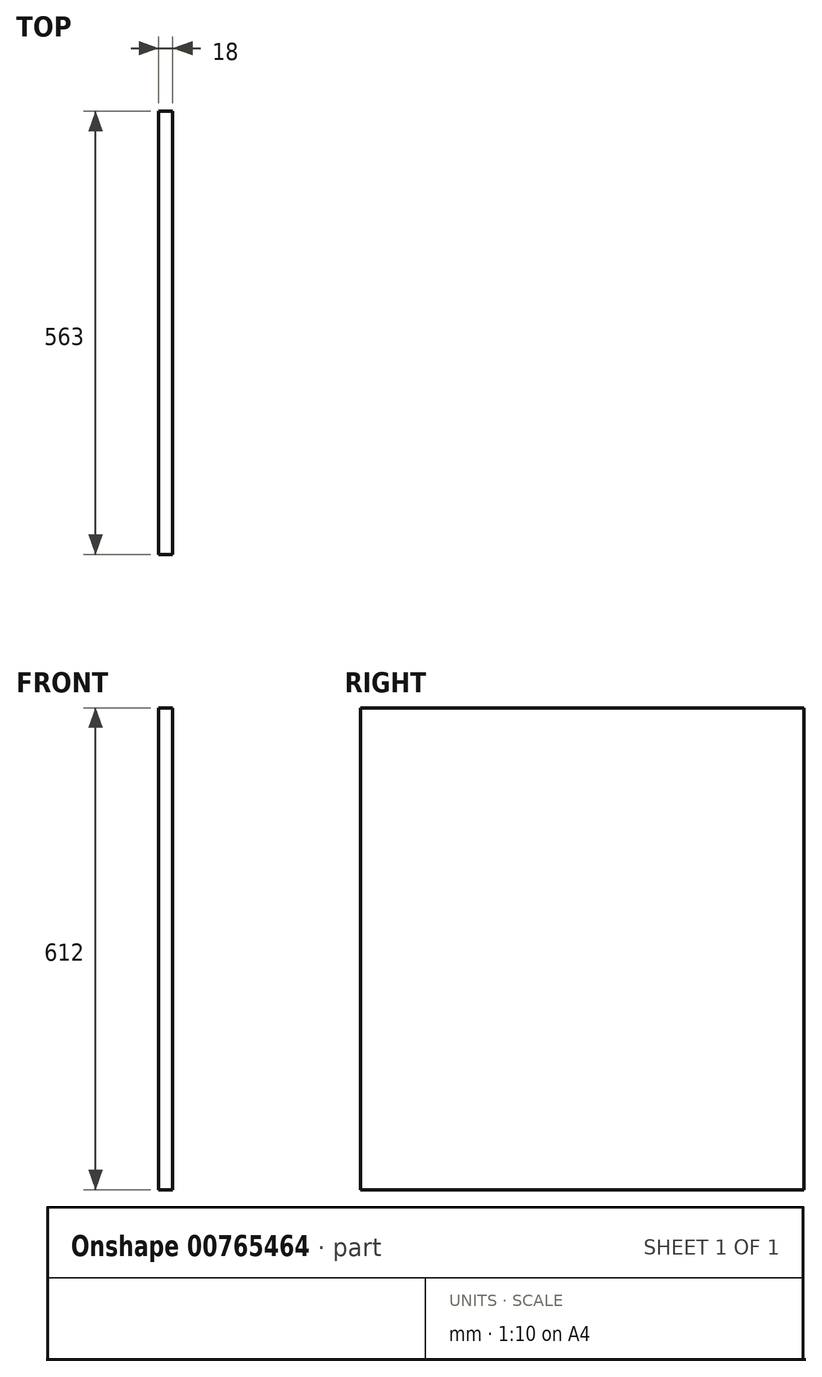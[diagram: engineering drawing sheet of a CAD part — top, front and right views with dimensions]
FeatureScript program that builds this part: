
annotation { "Feature Type Name" : "Feature", "Feature Type Description" : "" }
export const myFeature = defineFeature(function(context is Context, id is Id, definition is map)
    precondition{}
    {
        {
            var Q0;
            Q0=qCreatedBy(makeId("Right.planeOp"),FACE);
            var sketch = newSketch(context, id + "F0", { "sketchPlane" : qUnion([Q0])});
            skLineSegment(sketch, "E0.bottom", {"start": v(-281.5, 306) * mm, "end": v(281.5, 306) * mm});
            skLineSegment(sketch, "E0.top", {"start": v(-281.5, -306) * mm, "end": v(281.5, -306) * mm});
            skLineSegment(sketch, "E0.left", {"start": v(-281.5, 306) * mm, "end": v(-281.5, -306) * mm});
            skLineSegment(sketch, "E0.right", {"start": v(281.5, 306) * mm, "end": v(281.5, -306) * mm});
            skPoint(sketch, "E0.middle", {"position": v(0, 0) * mm});
            skSolve(sketch);
        }
        {
            var Q0;
            Q0 = qSketchRegion(id + "F0", true);
            extrude(context, id + "F1", {"entities" : qUnion([Q0]), "depth" : 18 * mm, "offsetDistance" : 25 * mm});
        }
    });
